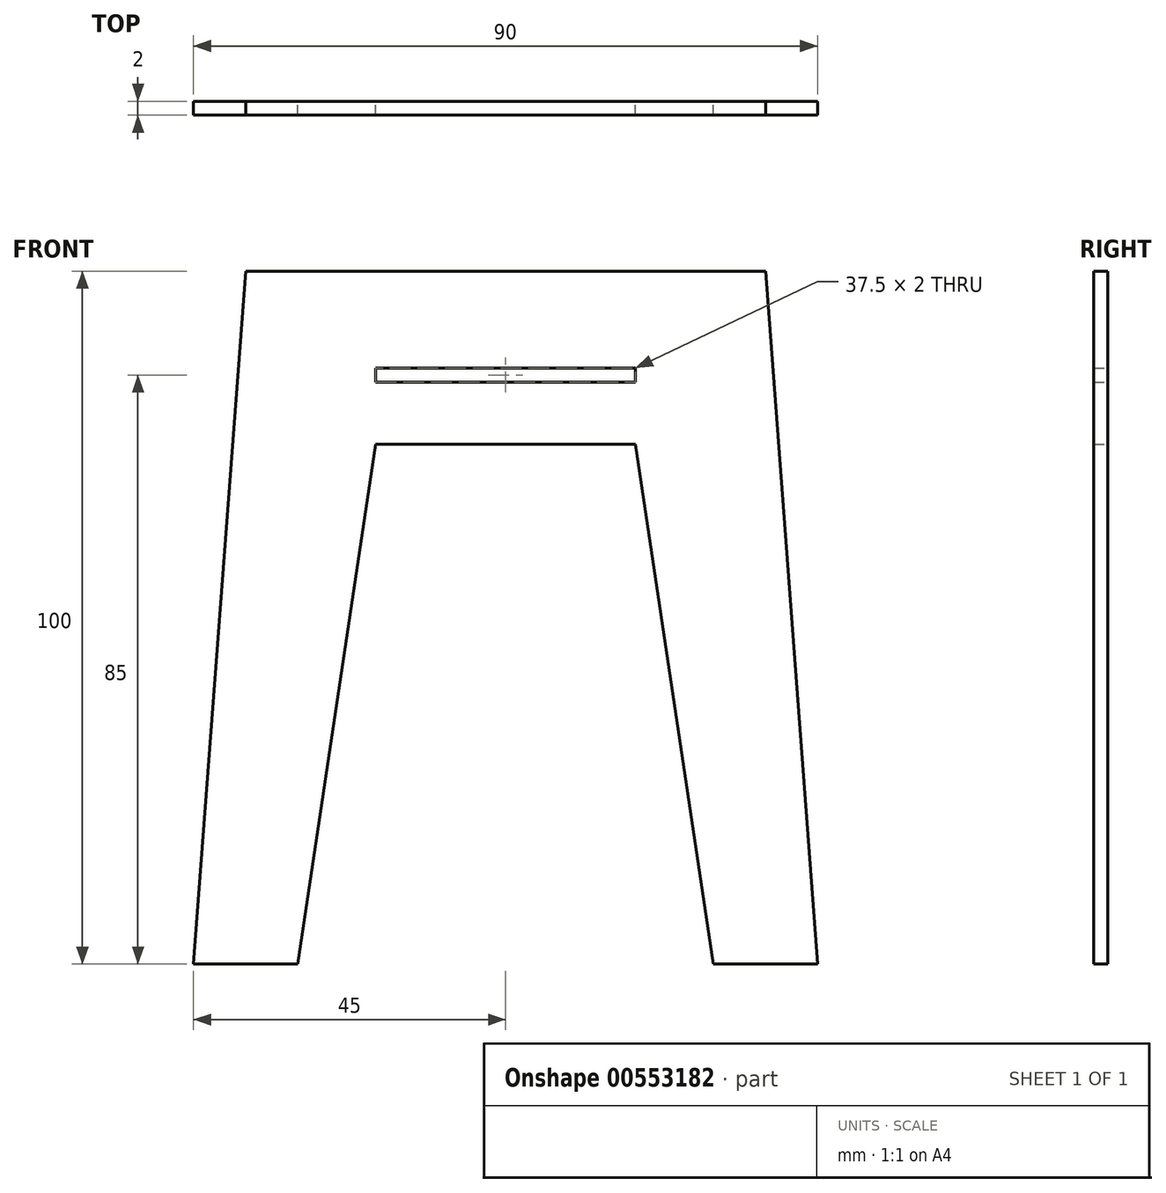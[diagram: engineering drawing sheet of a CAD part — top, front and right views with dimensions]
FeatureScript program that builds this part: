
annotation { "Feature Type Name" : "Feature", "Feature Type Description" : "" }
export const myFeature = defineFeature(function(context is Context, id is Id, definition is map)
    precondition{}
    {
        {
            var Q0;
            Q0=qCreatedBy(makeId("Front.planeOp"),FACE);
            var sketch = newSketch(context, id + "F0", { "sketchPlane" : qUnion([Q0])});
            skPoint(sketch, "E0.middle", {"position": v(0, 0) * mm});
            skLineSegment(sketch, "E1", {"start": v(-37.5, 50) * mm, "end": v(-45, -50) * mm});
            skLineSegment(sketch, "E2", {"start": v(37.5, 50) * mm, "end": v(45, -50) * mm});
            skLineSegment(sketch, "E3", {"start": v(-45, -50) * mm, "end": v(-30, -50) * mm});
            skLineSegment(sketch, "E4", {"start": v(45, -50) * mm, "end": v(30, -50) * mm});
            skPoint(sketch, "E5", {"position": v(18.75, 25) * mm});
            skPoint(sketch, "E6", {"position": v(-18.75, 25) * mm});
            skLineSegment(sketch, "E7", {"start": v(-18.75, 25) * mm, "end": v(-30, -50) * mm});
            skLineSegment(sketch, "E8", {"start": v(18.75, 25) * mm, "end": v(30, -50) * mm});
            skLineSegment(sketch, "E9", {"start": v(-18.75, 25) * mm, "end": v(18.75, 25) * mm});
            skLineSegment(sketch, "E10", {"start": v(-37.5, 50) * mm, "end": v(37.5, 50) * mm});
            skLineSegment(sketch, "E11", {"start": v(-18.75, 34) * mm, "end": v(18.75, 34) * mm});
            skLineSegment(sketch, "E12", {"start": v(18.75, 34) * mm, "end": v(18.75, 36) * mm});
            skLineSegment(sketch, "E13", {"start": v(18.75, 36) * mm, "end": v(-18.75, 36) * mm});
            skLineSegment(sketch, "E14", {"start": v(-18.75, 36) * mm, "end": v(-18.75, 34) * mm});
            skSolve(sketch);
        }
        {
            var Q0;
            Q0 = qSketchRegion(id + "F0", true);
            extrude(context, id + "F1", {"entities" : qUnion([Q0]), "depth" : 2 * mm, "offsetDistance" : 25 * mm});
        }
    });
